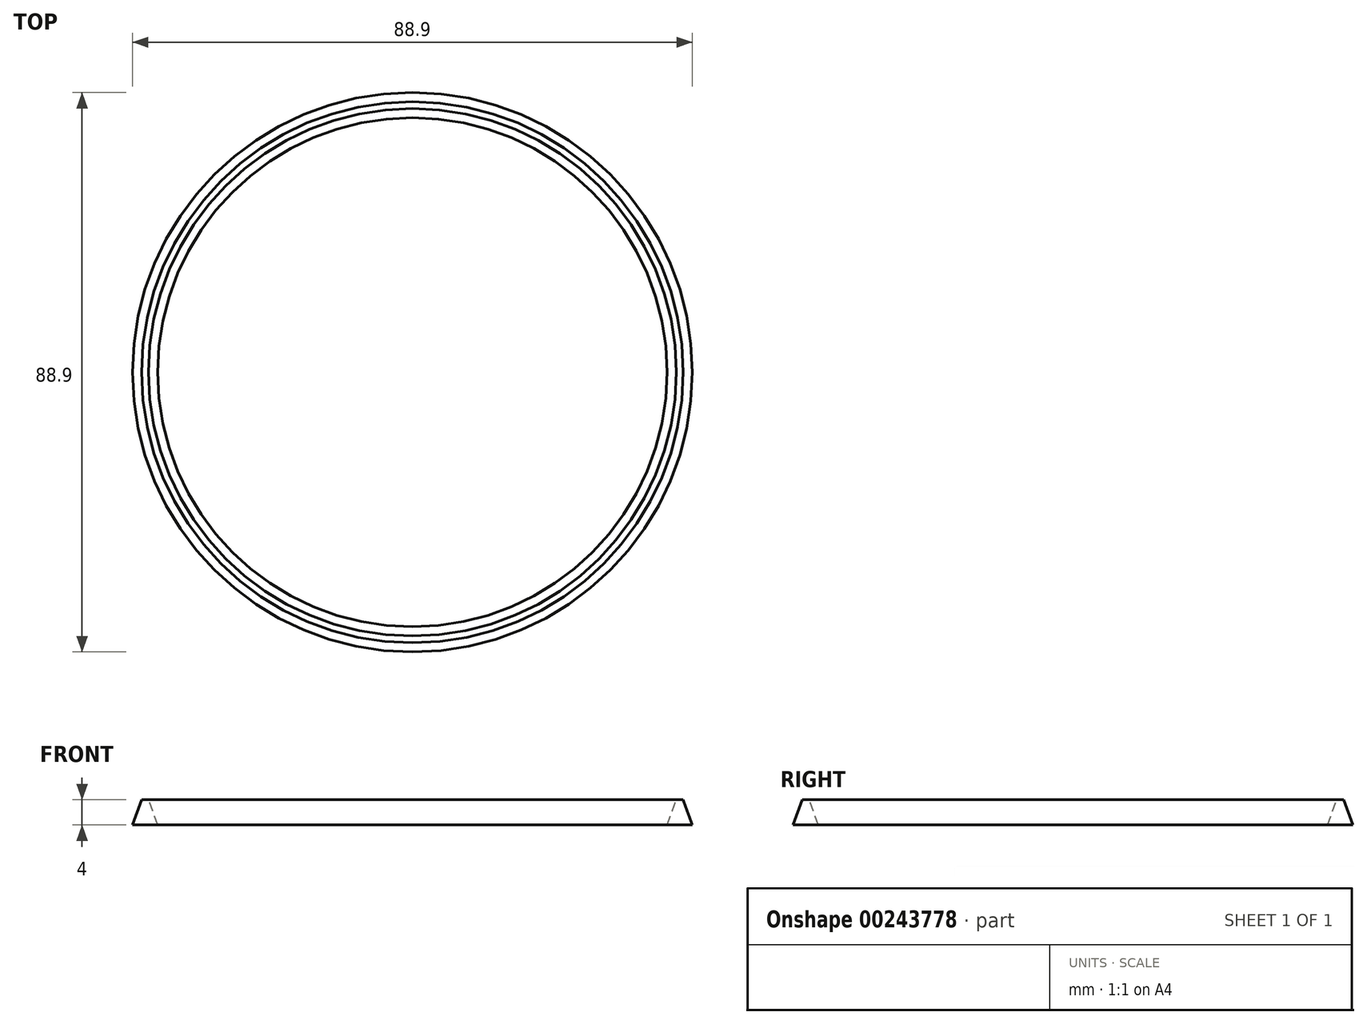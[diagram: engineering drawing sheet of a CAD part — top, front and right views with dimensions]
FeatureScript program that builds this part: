
annotation { "Feature Type Name" : "Feature", "Feature Type Description" : "" }
export const myFeature = defineFeature(function(context is Context, id is Id, definition is map)
    precondition{}
    {
        {
            var Q0;
            Q0=qCreatedBy(makeId("Top.planeOp"),FACE);
            var sketch = newSketch(context, id + "F0", { "sketchPlane" : qUnion([Q0])});
            skCircle(sketch, "E0", {"center": v(0, 0) * mm, "radius": 44.45 * mm});
            skCircle(sketch, "E1.0", {"center": v(0, 0) * mm, "radius": 40.45 * mm});
            skSolve(sketch);
        }
        {
            var Q0;
            Q0=makeQuery(id+"F0.imprint","IMPRINT",FACE,{"disambiguationData":[TD([[makeQuery(id+"F0.imprint","IMPRINT",EDGE,{"derivedFrom":sQuery(id+"F0.wireOp",EDGE,"E0")}),1.0]])]});
            extrude(context, id + "F1", {"entities" : qUnion([Q0]), "depth" : 4 * mm, "hasDraft" : true, "draftAngle" : 20 * degree, "draftPullDirection" : true});
        }
    });
